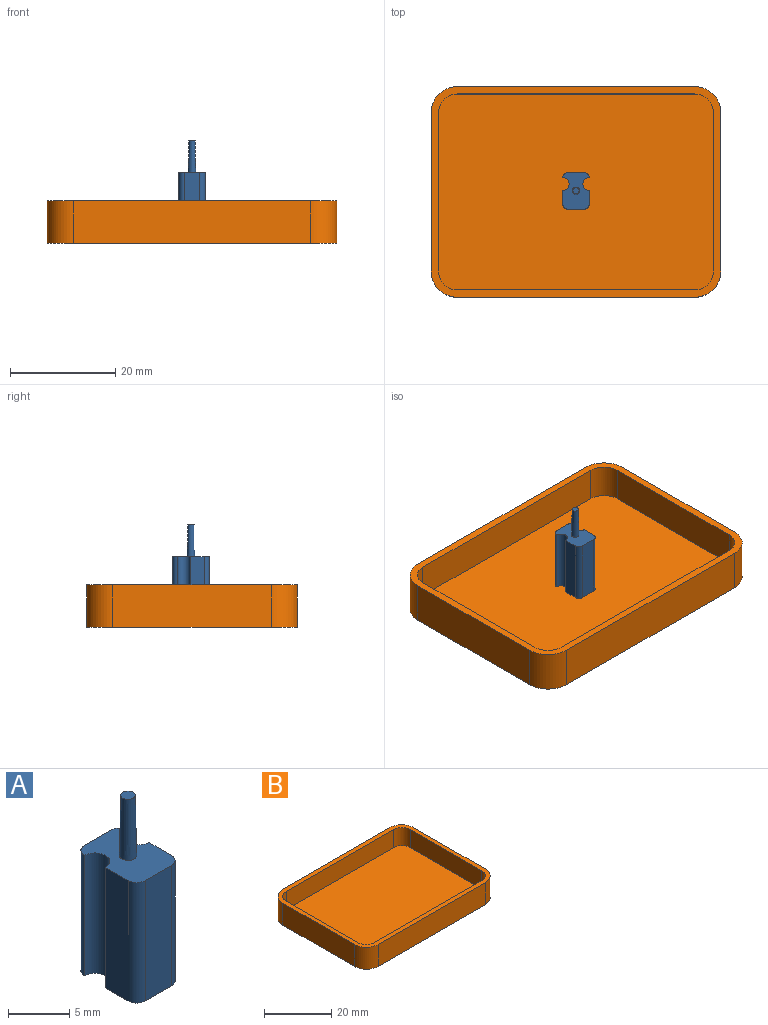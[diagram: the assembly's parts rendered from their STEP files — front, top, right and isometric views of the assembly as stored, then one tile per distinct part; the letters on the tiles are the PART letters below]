
ASSEMBLY  parts=2 mates=1
PART A: 14 faces, bbox 5x7x18 mm
  f0: cylinder r=1.2mm len=12mm, axis (0,0,-1), area 45.2mm2, adj f1,f9,f10,f11
  f1: cylinder r=1mm len=12mm, axis (0,0,-1), area 18.8mm2, adj f0,f2,f10,f11
  f2: plane 12x3mm, normal (0,1,0), area 36mm2, adj f1,f3,f10,f11
  f3: cylinder r=1mm len=12mm, axis (0,0,-1), area 18.8mm2, adj f2,f4,f10,f11
  f4: cylinder r=1.2mm len=12mm, axis (0,0,-1), area 45.2mm2, adj f3,f5,f10,f11
  f5: plane 12x2.6mm, normal (-1,0,0), area 31.2mm2, adj f4,f6,f10,f11
  f6: cylinder r=1mm len=12mm, axis (0,0,-1), area 18.8mm2, adj f5,f7,f10,f11
  f7: plane 12x3mm, normal (0,-1,0), area 36mm2, adj f6,f8,f10,f11
  f8: cylinder r=1mm len=12mm, axis (0,0,-1), area 18.8mm2, adj f7,f9,f10,f11
  f9: plane 12x2.6mm, normal (1,0,0), area 31.2mm2, adj f0,f8,f10,f11
  f10: plane 7x5mm, normal (0,0,1), area 28.1mm2, adj f0,f1,f2,f3,f4,f5,f6,f7
  f11: plane 7x5mm, normal (0,0,-1), area 29.6mm2, adj f0,f1,f2,f3,f4,f5,f6,f7
  f12: cone r=0.7mm half-angle=1deg, axis (0,0,-1), area 24.4mm2, adj f10,f13
  f13: plane 1.19x1.19mm, normal (0,0,1), area 1.1mm2, adj f12
PART B: 19 faces, bbox 55x40x8 mm
  f0: plane 55x40mm, normal (0,0,1), area 247.8mm2, adj f1,f2,f3,f4,f5,f6,f7,f8
  f1: plane 30x8mm, normal (1,0,0), area 240mm2, adj f0,f2,f8,f9
  f2: cylinder r=5mm len=8mm, axis (0,0,-1), area 62.8mm2, adj f0,f1,f3,f9
  f3: plane 45x8mm, normal (0,1,0), area 360mm2, adj f0,f2,f4,f9
  f4: cylinder r=5mm len=8mm, axis (0,0,-1), area 62.8mm2, adj f0,f3,f5,f9
  f5: plane 30x8mm, normal (-1,0,0), area 240mm2, adj f0,f4,f6,f9
  f6: cylinder r=5mm len=8mm, axis (0,0,-1), area 62.8mm2, adj f0,f5,f7,f9
  f7: plane 45x8mm, normal (0,-1,0), area 360mm2, adj f0,f6,f8,f9
  f8: cylinder r=5mm len=8mm, axis (0,0,-1), area 62.8mm2, adj f0,f1,f7,f9
  f9: plane 55x40mm, normal (0,0,-1), area 2178.5mm2, adj f1,f2,f3,f4,f5,f6,f7,f8
  f10: plane 30x6.6mm, normal (-1,0,0), area 198mm2, adj f0,f11,f17,f18
  f11: cylinder r=3.6mm len=6.6mm, axis (0,0,-1), area 37.3mm2, adj f0,f10,f12,f18
  f12: plane 45x6.6mm, normal (0,-1,0), area 297mm2, adj f0,f11,f13,f18
  f13: cylinder r=3.6mm len=6.6mm, axis (0,0,-1), area 37.3mm2, adj f0,f12,f14,f18
  f14: plane 30x6.6mm, normal (1,0,0), area 198mm2, adj f0,f13,f15,f18
  f15: cylinder r=3.6mm len=6.6mm, axis (0,0,-1), area 37.3mm2, adj f0,f14,f16,f18
  f16: plane 45x6.6mm, normal (0,1,0), area 297mm2, adj f0,f15,f17,f18
  f17: cylinder r=3.6mm len=6.6mm, axis (0,0,-1), area 37.3mm2, adj f0,f10,f16,f18
  f18: plane 52.2x37.2mm, normal (0,0,1), area 1930.7mm2, adj f10,f11,f12,f13,f14,f15,f16,f17
PLACE A t=(0,0.2,0)mm
PLACE B t=(0,0,-1.4)mm
MATE parallel B.f18 <-> A.f11  axis (0,0,1) through (0,0,0)mm
